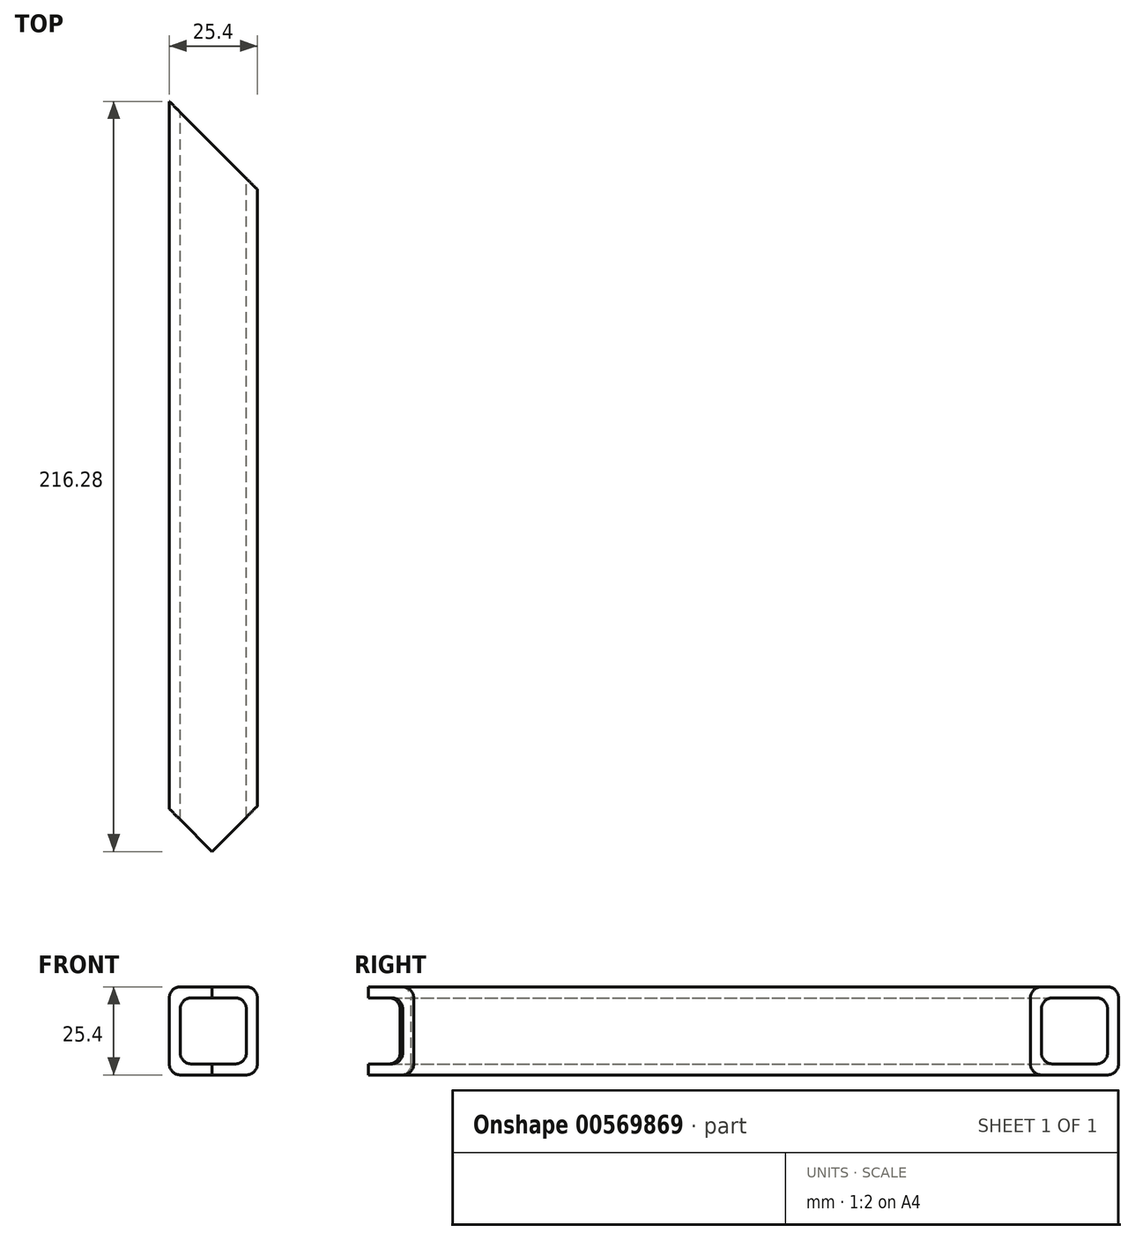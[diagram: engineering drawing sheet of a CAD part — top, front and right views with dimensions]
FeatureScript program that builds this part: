
annotation { "Feature Type Name" : "Feature", "Feature Type Description" : "" }
export const myFeature = defineFeature(function(context is Context, id is Id, definition is map)
    precondition{}
    {
        {
            var Q0;
            Q0=qCreatedBy(makeId("Front.planeOp"),FACE);
            var sketch = newSketch(context, id + "F0", { "sketchPlane" : qUnion([Q0])});
            skLineSegment(sketch, "E0.bottom", {"start": v(9.9, -12.8) * mm, "end": v(-9.15, -12.8) * mm});
            skLineSegment(sketch, "E0.top", {"start": v(9.9, 12.6) * mm, "end": v(-9.15, 12.6) * mm});
            skLineSegment(sketch, "E0.left", {"start": v(13.08, -9.62) * mm, "end": v(13.08, 9.43) * mm});
            skLineSegment(sketch, "E0.right", {"start": v(-12.32, -9.62) * mm, "end": v(-12.32, 9.43) * mm});
            skLineSegment(sketch, "E1.bottom", {"start": v(6.73, -9.62) * mm, "end": v(-5.97, -9.62) * mm});
            skLineSegment(sketch, "E1.top", {"start": v(6.73, 9.43) * mm, "end": v(-5.97, 9.43) * mm});
            skLineSegment(sketch, "E1.left", {"start": v(9.9, -6.44) * mm, "end": v(9.9, 6.26) * mm});
            skLineSegment(sketch, "E1.right", {"start": v(-9.15, -6.44) * mm, "end": v(-9.15, 6.26) * mm});
            skPoint(sketch, "E2.visualSharp", {"position": v(9.9, 9.43) * mm});
            skArc(sketch, "E2.filletArc", {"start": v(9.9, 6.26) * mm, "mid": v(8.97, 8.5) * mm, "end": v(6.73, 9.43) * mm});
            skPoint(sketch, "E3.visualSharp", {"position": v(-9.15, 9.43) * mm});
            skArc(sketch, "E3.filletArc", {"start": v(-5.97, 9.43) * mm, "mid": v(-8.22, 8.5) * mm, "end": v(-9.15, 6.26) * mm});
            skPoint(sketch, "E4.visualSharp", {"position": v(-9.15, -9.62) * mm});
            skArc(sketch, "E4.filletArc", {"start": v(-9.15, -6.44) * mm, "mid": v(-8.22, -8.69) * mm, "end": v(-5.97, -9.62) * mm});
            skPoint(sketch, "E5.visualSharp", {"position": v(9.9, -9.62) * mm});
            skArc(sketch, "E5.filletArc", {"start": v(6.73, -9.62) * mm, "mid": v(8.97, -8.69) * mm, "end": v(9.9, -6.44) * mm});
            skPoint(sketch, "E6.visualSharp", {"position": v(13.08, 12.6) * mm});
            skArc(sketch, "E6.filletArc", {"start": v(13.08, 9.43) * mm, "mid": v(12.15, 11.68) * mm, "end": v(9.9, 12.6) * mm});
            skPoint(sketch, "E7.visualSharp", {"position": v(-12.32, 12.6) * mm});
            skArc(sketch, "E7.filletArc", {"start": v(-9.15, 12.6) * mm, "mid": v(-11.4, 11.68) * mm, "end": v(-12.32, 9.43) * mm});
            skPoint(sketch, "E8.visualSharp", {"position": v(-12.32, -12.8) * mm});
            skArc(sketch, "E8.filletArc", {"start": v(-12.32, -9.62) * mm, "mid": v(-11.4, -11.86) * mm, "end": v(-9.15, -12.8) * mm});
            skPoint(sketch, "E9.visualSharp", {"position": v(13.08, -12.8) * mm});
            skArc(sketch, "E9.filletArc", {"start": v(9.9, -12.8) * mm, "mid": v(12.15, -11.86) * mm, "end": v(13.08, -9.62) * mm});
            skSolve(sketch);
        }
        {
            var Q0;
            Q0 = qSketchRegion(id + "F0", true);
            extrude(context, id + "F1", {"entities" : qUnion([Q0]), "depth" : 228.6 * mm, "offsetDistance" : 25.4 * mm});
        }
        {
            var Q0;
            Q0=makeQuery(id+"F1.opExtrude","SWEPT_FACE",FACE,{"disambiguationData":[OSD([sQuery(id+"F0.wireOp",EDGE,"E0.top")])]});
            var sketch = newSketch(context, id + "F2", { "sketchPlane" : qUnion([Q0])});
            skLineSegment(sketch, "E10", {"start": v(-12.32, 0) * mm, "end": v(13.08, -25.4) * mm});
            skLineSegment(sketch, "E11", {"start": v(13.08, -25.4) * mm, "end": v(13.08, 0) * mm});
            skLineSegment(sketch, "E12", {"start": v(13.08, 0) * mm, "end": v(-12.32, 0) * mm});
            skSolve(sketch);
        }
        {
            var Q0;
            Q0 = qSketchRegion(id + "F2", true);
            extrude(context, id + "F3", {"entities" : qUnion([Q0]), "operationType" : NewBodyOperationType.REMOVE, "oppositeDirection" : true, "depth" : 25.4 * mm, "offsetDistance" : 25.4 * mm});
        }
        {
            var Q0;
            Q0=makeQuery(id+"F1.opExtrude","SWEPT_FACE",FACE,{"disambiguationData":[OSD([sQuery(id+"F0.wireOp",EDGE,"E0.bottom")])]});
            var sketch = newSketch(context, id + "F4", { "sketchPlane" : qUnion([Q0])});
            skLineSegment(sketch, "E13", {"start": v(-12.32, 228.6) * mm, "end": v(13.08, 203.2) * mm});
            skLineSegment(sketch, "E14", {"start": v(13.08, 203.2) * mm, "end": v(13.08, 228.6) * mm});
            skLineSegment(sketch, "E15", {"start": v(13.08, 228.6) * mm, "end": v(-12.32, 228.6) * mm});
            skSolve(sketch);
        }
        {
            var Q0;
            Q0 = qSketchRegion(id + "F4", true);
            extrude(context, id + "F5", {"entities" : qUnion([Q0]), "operationType" : NewBodyOperationType.REMOVE, "oppositeDirection" : true, "depth" : 25.4 * mm, "offsetDistance" : 25.4 * mm});
        }
        {
            var Q0;
            Q0=makeQuery(id+"F1.opExtrude","SWEPT_FACE",FACE,{"disambiguationData":[OSD([sQuery(id+"F0.wireOp",EDGE,"E0.bottom")])]});
            var sketch = newSketch(context, id + "F6", { "sketchPlane" : qUnion([Q0])});
            skLineSegment(sketch, "E16", {"start": v(0, 216.28) * mm, "end": v(-40.98, 175.3) * mm});
            skLineSegment(sketch, "E17", {"start": v(-40.98, 175.3) * mm, "end": v(-40.98, 257.26) * mm});
            skLineSegment(sketch, "E18", {"start": v(-40.98, 257.26) * mm, "end": v(0, 216.28) * mm});
            skSolve(sketch);
        }
        {
            var Q0;
            Q0 = qSketchRegion(id + "F6", true);
            extrude(context, id + "F7", {"entities" : qUnion([Q0]), "operationType" : NewBodyOperationType.REMOVE, "oppositeDirection" : true, "depth" : 25.4 * mm, "offsetDistance" : 25.4 * mm});
        }
    });
